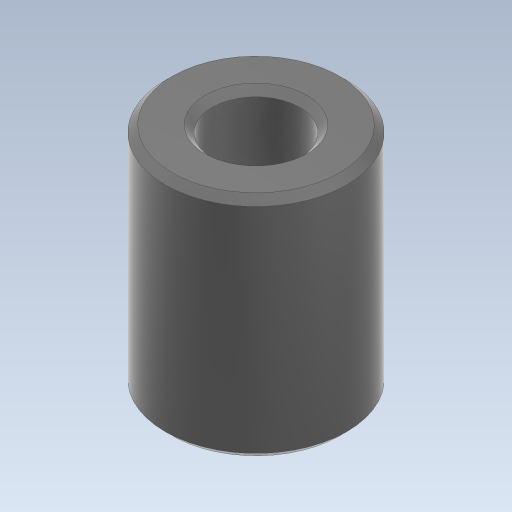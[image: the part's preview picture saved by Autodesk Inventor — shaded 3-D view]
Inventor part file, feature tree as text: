
AUTODESK INVENTOR PART (.ipt)
format: ipt  version: 2023 (Build 270158000, 158)  size: 307,712 bytes
history: native  units: mm
features: extrude x1, chamfer x1, sketch x1
ambient origin geometry x8: Origin, YZ Plane, XZ Plane, XY Plane, X Axis, Y Axis, Z Axis, Center Point
bodies: Solid1 (feature_tree)
feature tree (3):
  extrude  "Extrusion1"  Depth=13.0mm
  chamfer  "Chamfer1"  Distance=13.0mm
  sketch  "Sketch1"  dims[d0=5.0mm d1=10.35mm d2=13.0mm d3=0.0mm d4=0.4mm d5=2.0mm d6=45.0deg]
